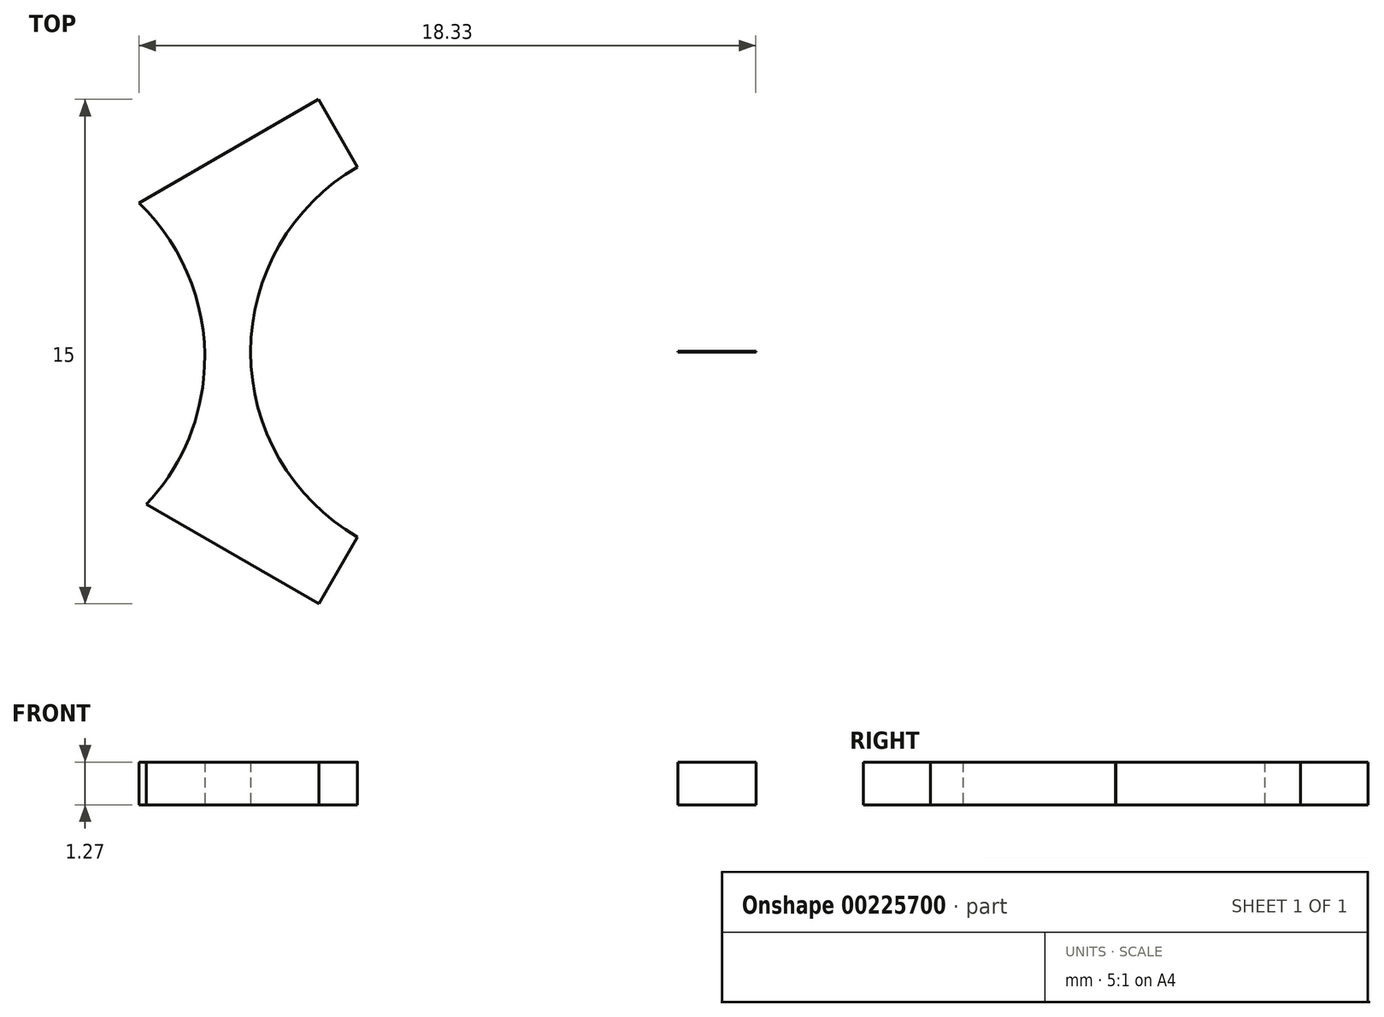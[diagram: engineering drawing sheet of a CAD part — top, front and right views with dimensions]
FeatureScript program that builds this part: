
annotation { "Feature Type Name" : "Feature", "Feature Type Description" : "" }
export const myFeature = defineFeature(function(context is Context, id is Id, definition is map)
    precondition{}
    {
        {
            var Q0;
            Q0=qCreatedBy(makeId("Top.planeOp"),FACE);
            var sketch = newSketch(context, id + "F0", { "sketchPlane" : qUnion([Q0])});
            skCircle(sketch, "E0", {"center": v(0, 0) * mm, "radius": 6.35 * mm});
            skLineSegment(sketch, "E1", {"start": v(0, 0) * mm, "end": v(-1.64, 6.13) * mm, "construction": true});
            skLineSegment(sketch, "E2", {"start": v(0, 0) * mm, "end": v(-6.13, -1.64) * mm, "construction": true});
            skLineSegment(sketch, "E3", {"start": v(0, 0) * mm, "end": v(1.64, -6.13) * mm, "construction": true});
            skLineSegment(sketch, "E4", {"start": v(0, 0) * mm, "end": v(6.13, 1.64) * mm, "construction": true});
            skPoint(sketch, "E5.center", {"position": v(-1.38, -0.8) * mm});
            skLineSegment(sketch, "E6", {"start": v(0, 0) * mm, "end": v(-23.38, -40.48) * mm});
            skLineSegment(sketch, "E7.1.0", {"start": v(0, 0) * mm, "end": v(46.75, -0.01) * mm});
            skLineSegment(sketch, "E7.2.0", {"start": v(0, 0) * mm, "end": v(-23.36, 40.5) * mm});
            skLineSegment(sketch, "E8", {"start": v(1.02, -10.57) * mm, "end": v(-4.33, -7.49) * mm});
            skLineSegment(sketch, "E9", {"start": v(-4.33, -7.49) * mm, "end": v(-9.45, -4.53) * mm});
            skLineSegment(sketch, "E10", {"start": v(-9.45, -4.53) * mm, "end": v(-23.38, -40.48) * mm});
            skLineSegment(sketch, "E11", {"start": v(1.02, -10.57) * mm, "end": v(-23.38, -40.48) * mm});
            skLineSegment(sketch, "E12.1.0", {"start": v(8.66, 0.02) * mm, "end": v(8.66, -5.9) * mm});
            skLineSegment(sketch, "E12.1.1", {"start": v(8.66, -5.9) * mm, "end": v(46.76, 0) * mm});
            skLineSegment(sketch, "E12.1.2", {"start": v(8.67, 6.19) * mm, "end": v(46.76, 0) * mm});
            skLineSegment(sketch, "E12.1.3", {"start": v(8.67, 6.19) * mm, "end": v(8.66, 0.02) * mm});
            skLineSegment(sketch, "E12.2.0", {"start": v(-4.33, 7.52) * mm, "end": v(0.8, 10.47) * mm});
            skLineSegment(sketch, "E12.2.1", {"start": v(0.8, 10.47) * mm, "end": v(-23.37, 40.52) * mm});
            skLineSegment(sketch, "E12.2.2", {"start": v(-9.67, 4.43) * mm, "end": v(-23.37, 40.52) * mm});
            skLineSegment(sketch, "E12.2.3", {"start": v(-9.67, 4.43) * mm, "end": v(-4.33, 7.52) * mm});
            skPoint(sketch, "E12.center", {"position": v(0, 0.02) * mm});
            skLineSegment(sketch, "E13", {"start": v(-1.38, -0.8) * mm, "end": v(-7.75, -0.8) * mm});
            skArc(sketch, "E14", {"start": v(-9.45, -4.53) * mm, "mid": v(-8.29, -2.8) * mm, "end": v(-7.75, -0.8) * mm});
            skArc(sketch, "E15.1.0", {"start": v(8.65, -5.92) * mm, "mid": v(6.57, -5.78) * mm, "end": v(4.56, -6.3) * mm});
            skArc(sketch, "E15.2.0", {"start": v(0.8, 10.45) * mm, "mid": v(1.72, 8.58) * mm, "end": v(3.18, 7.1) * mm});
            skArc(sketch, "E16", {"start": v(-7.75, -0.8) * mm, "mid": v(-8.1, 2.04) * mm, "end": v(-9.67, 4.43) * mm});
            skArc(sketch, "E17.1.0", {"start": v(4.56, -6.3) * mm, "mid": v(2.29, -8.04) * mm, "end": v(1, -10.6) * mm});
            skArc(sketch, "E17.2.0", {"start": v(3.18, 7.1) * mm, "mid": v(5.82, 6) * mm, "end": v(8.68, 6.16) * mm});
            skLineSegment(sketch, "E18", {"start": v(8.66, 0.02) * mm, "end": v(6.35, 0.02) * mm});
            skSolve(sketch);
        }
        {
            var Q0;
            {var subQ0=sQuery(id+"F0.wireOp",EDGE,"E7.2.0");var subQ1=sQuery(id+"F0.wireOp",EDGE,"E0");var subQ2=makeQuery(id+"F0.imprint","INTERSECT",VERTEX,{"derivedFrom":[subQ1,subQ0]});Q0=makeQuery(id+"F0.imprint","IMPRINT",FACE,{"disambiguationData":[TD([[makeQuery(id+"F0.imprint","IMPRINT",EDGE,{"disambiguationData":[TD([[subQ2,-1.0]])],"derivedFrom":subQ1}),-1.0]])]});}
            var Q1;
            {var subQ3=sQuery(id+"F0.wireOp",EDGE,"E17.2.0");var subQ6=sQuery(id+"F0.wireOp",EDGE,"E0");var subQ9=makeQuery(id+"F0.imprint","INTERSECT",VERTEX,{"disambiguationData":[OD(1.0)],"derivedFrom":[subQ6,subQ3]});Q1=makeQuery(id+"F0.imprint","IMPRINT",FACE,{"disambiguationData":[TD([[makeQuery(id+"F0.imprint","IMPRINT",EDGE,{"disambiguationData":[TD([[subQ9,1.0]])],"derivedFrom":subQ6}),-1.0]])]});}
            var Q2;
            {var subQ0=sQuery(id+"F0.wireOp",EDGE,"E17.1.0");var subQ1=sQuery(id+"F0.wireOp",EDGE,"E0");var subQ2=makeQuery(id+"F0.imprint","INTERSECT",VERTEX,{"disambiguationData":[OD(1.0)],"derivedFrom":[subQ1,subQ0]});Q2=makeQuery(id+"F0.imprint","IMPRINT",FACE,{"disambiguationData":[TD([[makeQuery(id+"F0.imprint","IMPRINT",EDGE,{"disambiguationData":[TD([[subQ2,1.0]])],"derivedFrom":subQ1}),-1.0]])]});}
            var Q3;
            {var subQ4=sQuery(id+"F0.wireOp",EDGE,"E9");Q3=makeQuery(id+"F0.imprint","IMPRINT",FACE,{"disambiguationData":[TD([[makeQuery(id+"F0.imprint","IMPRINT",EDGE,{"derivedFrom":subQ4}),-1.0]])]});}
            extrude(context, id + "F1", {"entities" : qUnion([Q0, Q1, Q2, Q3]), "depth" : 1.27 * mm});
        }
    });
